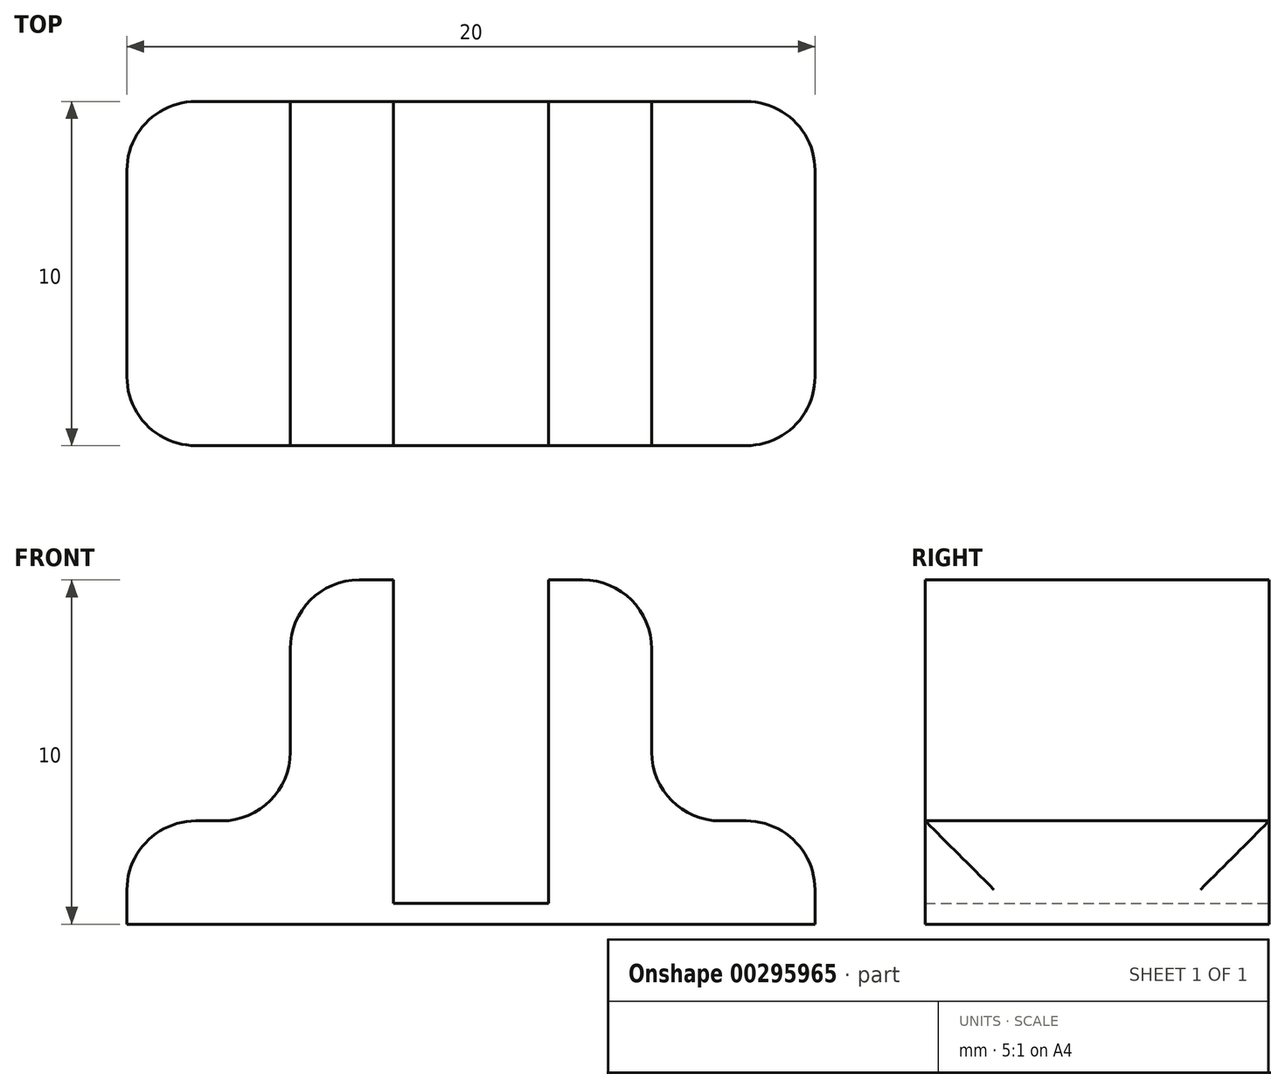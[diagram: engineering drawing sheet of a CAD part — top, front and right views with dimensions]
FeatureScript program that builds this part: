
annotation { "Feature Type Name" : "Feature", "Feature Type Description" : "" }
export const myFeature = defineFeature(function(context is Context, id is Id, definition is map)
    precondition{}
    {
        {
            var Q0;
            Q0=qCreatedBy(makeId("Front.planeOp"),FACE);
            var sketch = newSketch(context, id + "F0", { "sketchPlane" : qUnion([Q0])});
            skLineSegment(sketch, "E0", {"start": v(-2.25, 0.6) * mm, "end": v(-2.25, 10) * mm});
            skLineSegment(sketch, "E1", {"start": v(-2.25, 10) * mm, "end": v(-5.25, 10) * mm});
            skLineSegment(sketch, "E2", {"start": v(-5.25, 10) * mm, "end": v(-5.25, 3) * mm});
            skLineSegment(sketch, "E3", {"start": v(-5.25, 3) * mm, "end": v(-10, 3) * mm});
            skLineSegment(sketch, "E4", {"start": v(-10, 3) * mm, "end": v(-10, 0) * mm});
            skLineSegment(sketch, "E5", {"start": v(-10, 0) * mm, "end": v(0, 0) * mm});
            skLineSegment(sketch, "E6", {"start": v(0, 0) * mm, "end": v(0, 0.6) * mm});
            skLineSegment(sketch, "E7", {"start": v(0, 0.6) * mm, "end": v(-2.25, 0.6) * mm});
            skLineSegment(sketch, "E8.MirrorCS", {"start": v(0, 0.6) * mm, "end": v(2.25, 0.6) * mm});
            skLineSegment(sketch, "E9.MirrorCS", {"start": v(5.25, 3) * mm, "end": v(10, 3) * mm});
            skLineSegment(sketch, "E10.MirrorCS", {"start": v(10, 0) * mm, "end": v(0, 0) * mm});
            skLineSegment(sketch, "E11.MirrorCS", {"start": v(5.25, 10) * mm, "end": v(5.25, 3) * mm});
            skLineSegment(sketch, "E12.MirrorCS", {"start": v(10, 3) * mm, "end": v(10, 0) * mm});
            skLineSegment(sketch, "E13.MirrorCS", {"start": v(2.25, 0.6) * mm, "end": v(2.25, 10) * mm});
            skLineSegment(sketch, "E14.MirrorCS", {"start": v(2.25, 10) * mm, "end": v(5.25, 10) * mm});
            skSolve(sketch);
        }
        {
            var Q0;
            Q0 = qSketchRegion(id + "F0", true);
            extrude(context, id + "F1", {"entities" : qUnion([Q0]), "depth" : 10 * mm, "offsetDistance" : 25 * mm});
        }
        {
            var Q0;
            Q0=makeQuery(id+"F1.opExtrude","SWEPT_EDGE",EDGE,{"disambiguationData":[OSD([sQuery(id+"F0.wireOp",EDGE,"E2"),sQuery(id+"F0.wireOp",EDGE,"E3")])]});
            var Q1;
            Q1=makeQuery(id+"F1.opExtrude","SWEPT_EDGE",EDGE,{"disambiguationData":[OSD([sQuery(id+"F0.wireOp",EDGE,"E9.MirrorCS"),sQuery(id+"F0.wireOp",EDGE,"E11.MirrorCS")])]});
            var Q2;
            Q2=makeQuery(id+"F1.opExtrude","SWEPT_EDGE",EDGE,{"disambiguationData":[OSD([sQuery(id+"F0.wireOp",EDGE,"E9.MirrorCS"),sQuery(id+"F0.wireOp",EDGE,"E12.MirrorCS")])]});
            var Q3;
            Q3=makeQuery(id+"F1.opExtrude","SWEPT_EDGE",EDGE,{"disambiguationData":[OSD([sQuery(id+"F0.wireOp",EDGE,"E11.MirrorCS"),sQuery(id+"F0.wireOp",EDGE,"E14.MirrorCS")])]});
            var Q4;
            Q4=makeQuery(id+"F1.opExtrude","SWEPT_EDGE",EDGE,{"disambiguationData":[OSD([sQuery(id+"F0.wireOp",EDGE,"E1"),sQuery(id+"F0.wireOp",EDGE,"E2")])]});
            var Q5;
            Q5=makeQuery(id+"F1.opExtrude","SWEPT_EDGE",EDGE,{"disambiguationData":[OSD([sQuery(id+"F0.wireOp",EDGE,"E3"),sQuery(id+"F0.wireOp",EDGE,"E4")])]});
            var Q6;
            Q6=makeQuery(id+"F1.opExtrude","CAP_EDGE",EDGE,{"disambiguationData":[OSD([sQuery(id+"F0.wireOp",EDGE,"E4")])],"isStart":false});
            var Q7;
            Q7=makeQuery(id+"F1.opExtrude","CAP_EDGE",EDGE,{"disambiguationData":[OSD([sQuery(id+"F0.wireOp",EDGE,"E4")])],"isStart":true});
            var Q8;
            Q8=makeQuery(id+"F1.opExtrude","CAP_EDGE",EDGE,{"disambiguationData":[OSD([sQuery(id+"F0.wireOp",EDGE,"E12.MirrorCS")])],"isStart":false});
            var Q9;
            Q9=makeQuery(id+"F1.opExtrude","CAP_EDGE",EDGE,{"disambiguationData":[OSD([sQuery(id+"F0.wireOp",EDGE,"E12.MirrorCS")])],"isStart":true});
            fillet(context, id + "F2", {"entities" : qUnion([Q0, Q1, Q2, Q3, Q4, Q5, Q6, Q7, Q8, Q9]), "tangentPropagation" : true, "radius" : 2 * mm, "defaultsChanged" : false, "vertexSettings" : [], "allowEdgeOverflow" : false});
        }
    });
